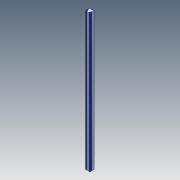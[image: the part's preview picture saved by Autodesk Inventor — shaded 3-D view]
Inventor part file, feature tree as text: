
AUTODESK INVENTOR PART (.ipt)
format: ipt  version: 2020 (Build 240168000, 168)  size: 361,472 bytes
history: native  units: mm
features: other x4, projected_geometry x3, extrude x2, sketch x2
ambient origin geometry x8: Origin, YZ Plane, XZ Plane, XY Plane, X Axis, Y Axis, Z Axis, Center Point
bodies: Body1 (feature_tree), Body2 (feature_tree)
feature tree (11):
  other  "ソリッド1"
  extrude  "押し出し1"  Depth=1200.0mm TaperAngle=0.0deg
  extrude  "押し出し2"  Depth=672.0mm TaperAngle=0.0deg
  other  "ソリッド2"
  sketch  "スケッチ1"
  projected_geometry  "投影ループ1"
  projected_geometry  "投影ループ2"
  sketch  "スケッチ2"
  projected_geometry  "投影ループ3"
  other  "Boss-Extrude1[1]"
  other  "Boss-Extrude1[2]"
